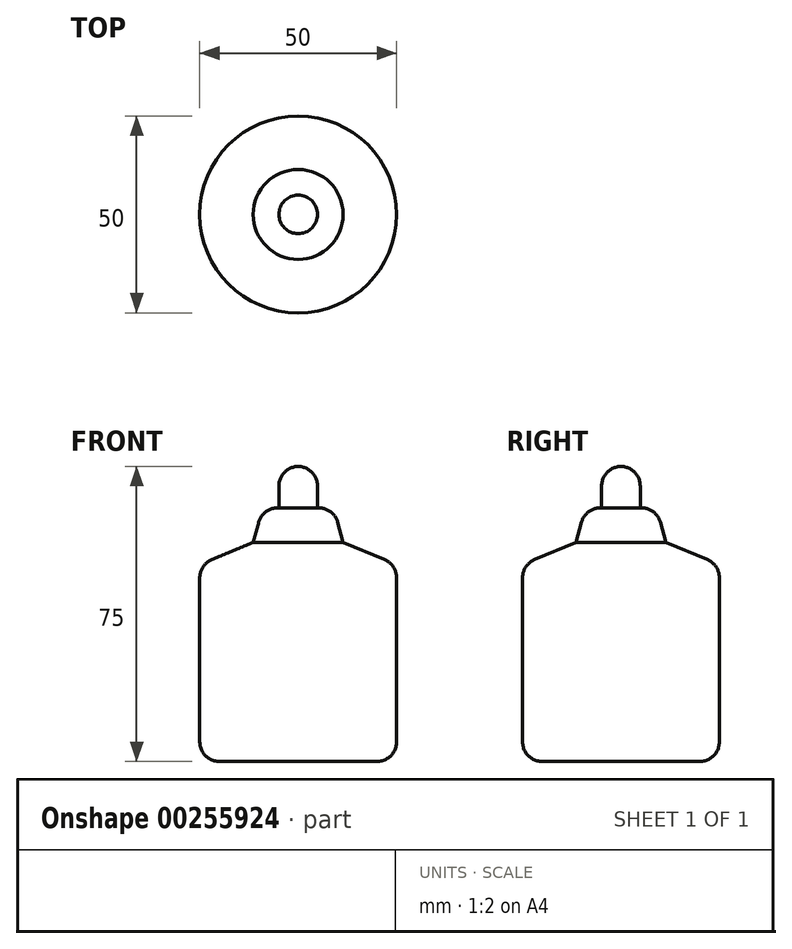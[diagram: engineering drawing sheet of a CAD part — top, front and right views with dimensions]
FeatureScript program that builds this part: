
annotation { "Feature Type Name" : "Feature", "Feature Type Description" : "" }
export const myFeature = defineFeature(function(context is Context, id is Id, definition is map)
    precondition{}
    {
        {
            var Q0;
            Q0=qCreatedBy(makeId("Front.planeOp"),FACE);
            var sketch = newSketch(context, id + "F0", { "sketchPlane" : qUnion([Q0])});
            skLineSegment(sketch, "E0", {"start": v(0, 0) * mm, "end": v(0, 75) * mm});
            skLineSegment(sketch, "E1", {"start": v(0, 0) * mm, "end": v(25, 0) * mm});
            skLineSegment(sketch, "E2", {"start": v(25, 0) * mm, "end": v(25, 50) * mm});
            skLineSegment(sketch, "E3", {"start": v(25, 50) * mm, "end": v(11.42, 55.71) * mm});
            skLineSegment(sketch, "E4", {"start": v(11.42, 55.71) * mm, "end": v(9, 64.46) * mm});
            skLineSegment(sketch, "E5", {"start": v(9, 64.46) * mm, "end": v(4.9, 64.46) * mm});
            skLineSegment(sketch, "E6", {"start": v(4.9, 64.46) * mm, "end": v(4.9, 74.48) * mm});
            skLineSegment(sketch, "E7", {"start": v(4.9, 74.48) * mm, "end": v(0, 75) * mm});
            skSolve(sketch);
        }
        {
            var Q0;
            Q0=makeQuery(id+"F0.imprint","IMPRINT",FACE,{"disambiguationData":[TD([[makeQuery(id+"F0.imprint","IMPRINT",EDGE,{"derivedFrom":sQuery(id+"F0.wireOp",EDGE,"E0")}),-1.0]])]});
            var sketch = newSketch(context, id + "F1", { "sketchPlane" : qUnion([Q0])});
            skSolve(sketch);
        }
        {
            var Q0;
            Q0=makeQuery(id+"F1.imprint","IMPRINT",FACE,{"disambiguationData":[TD([[makeQuery(id+"F1.imprint","IMPRINT",EDGE,{"derivedFrom":makeQuery(id+"F0.imprint","IMPRINT",EDGE,{"derivedFrom":sQuery(id+"F0.wireOp",EDGE,"E0")})}),-1.0]])]});
            var Q1;
            Q1=sQuery(id+"F0.wireOp",EDGE,"E0");
            revolve(context, id + "F2", {"entities" : qUnion([Q0]), "axis" : qUnion([Q1]), "revolveType" : RevolveType.FULL});
        }
        {
            var Q0;
            Q0=makeQuery(id+"F2.opRevolve","SWEPT_EDGE",EDGE,{"disambiguationData":[OSD([sQuery(id+"F0.wireOp",EDGE,"E2"),sQuery(id+"F0.wireOp",EDGE,"E3")])]});
            var Q1;
            Q1=makeQuery(id+"F2.opRevolve","SWEPT_FACE",FACE,{"disambiguationData":[OSD([sQuery(id+"F0.wireOp",EDGE,"E2")])]});
            var Q2;
            Q2=makeQuery(id+"F2.opRevolve","SWEPT_EDGE",EDGE,{"disambiguationData":[OSD([sQuery(id+"F0.wireOp",EDGE,"E4"),sQuery(id+"F0.wireOp",EDGE,"E5")])]});
            var Q3;
            Q3=makeQuery(id+"F2.opRevolve","SWEPT_EDGE",EDGE,{"disambiguationData":[OSD([sQuery(id+"F0.wireOp",EDGE,"E6"),sQuery(id+"F0.wireOp",EDGE,"E7")])]});
            fillet(context, id + "F3", {"entities" : qUnion([Q0, Q1, Q2, Q3]), "radius" : 5 * mm, "tangentPropagation" : true, "allowEdgeOverflow" : false});
        }
    });
